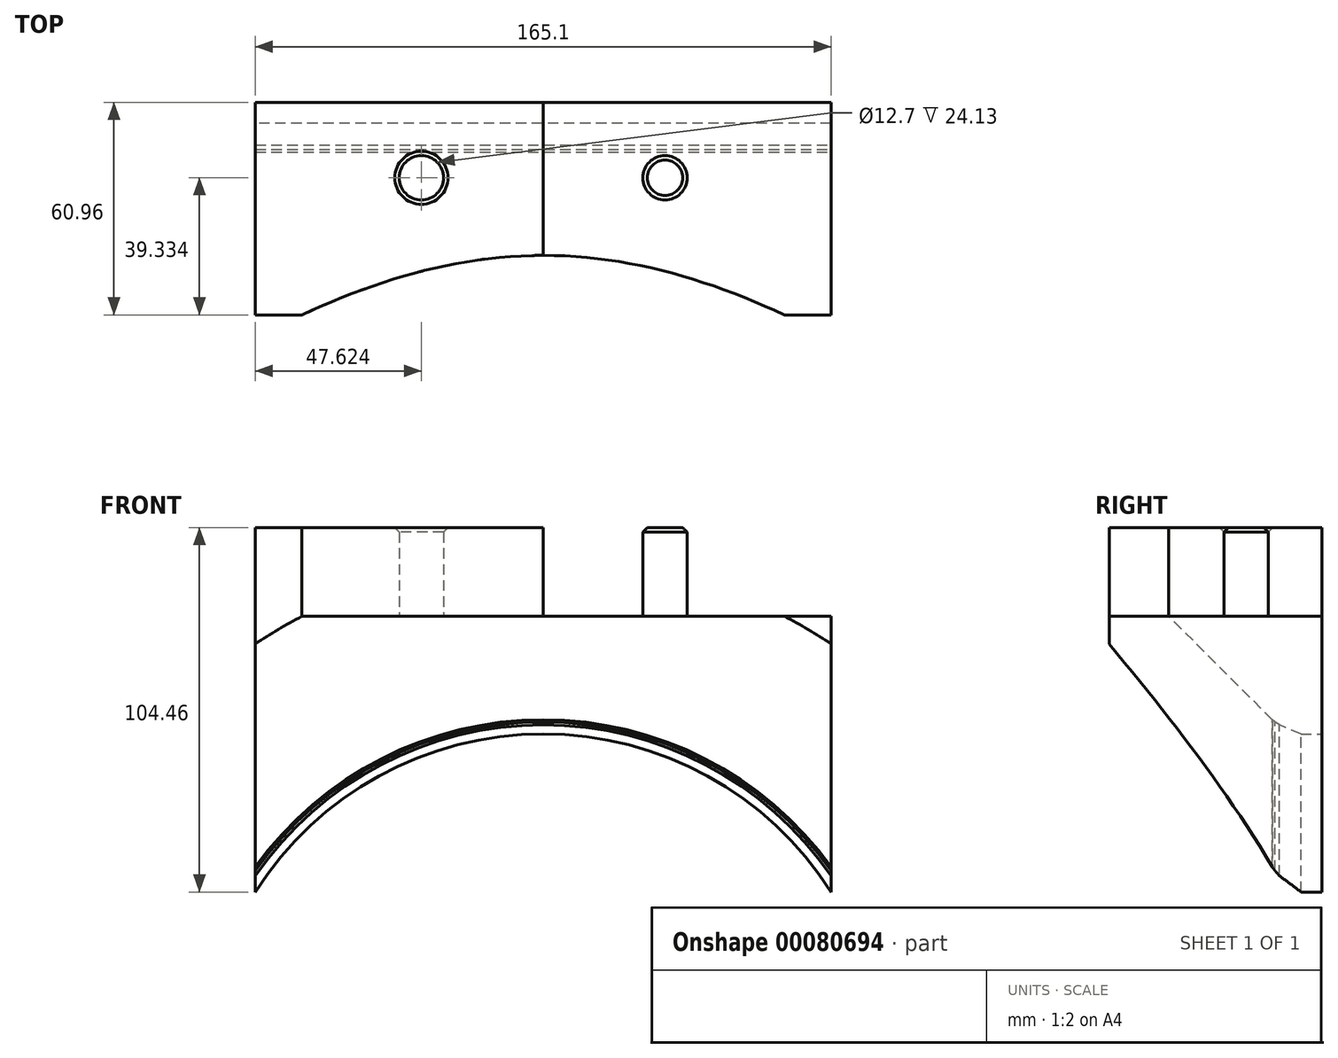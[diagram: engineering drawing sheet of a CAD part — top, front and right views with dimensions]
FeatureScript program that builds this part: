
annotation { "Feature Type Name" : "Feature", "Feature Type Description" : "" }
export const myFeature = defineFeature(function(context is Context, id is Id, definition is map)
    precondition{}
    {
        {
            var Q0;
            Q0=qCreatedBy(makeId("Front.planeOp"),FACE);
            var sketch = newSketch(context, id + "F0", { "sketchPlane" : qUnion([Q0])});
            skLineSegment(sketch, "E0", {"start": v(0, 54.45) * mm, "end": v(-96.4, 54.45) * mm});
            skLineSegment(sketch, "E1", {"start": v(-96.4, 54.45) * mm, "end": v(68.7, 54.45) * mm});
            skLineSegment(sketch, "E2", {"start": v(68.7, 54.45) * mm, "end": v(68.7, -24.61) * mm});
            skLineSegment(sketch, "E3", {"start": v(-96.4, 54.45) * mm, "end": v(-96.4, -24.61) * mm});
            skArc(sketch, "E4", {"start": v(68.7, -24.61) * mm, "mid": v(-13.85, 20.72) * mm, "end": v(-96.4, -24.61) * mm});
            skSolve(sketch);
        }
        {
            var Q0;
            {var subQ2=sQuery(id+"F0.wireOp",EDGE,"E2");Q0=makeQuery(id+"F0.imprint","IMPRINT",FACE,{"disambiguationData":[TD([[makeQuery(id+"F0.imprint","IMPRINT",EDGE,{"derivedFrom":subQ2}),-1.0]])]});}
            extrude(context, id + "F1", {"entities" : qUnion([Q0]), "depth" : 60.96 * mm});
        }
        {
            var Q0;
            Q0=makeQuery(id+"F1.opExtrude","CAP_EDGE",EDGE,{"disambiguationData":[OSD([sQuery(id+"F0.wireOp",EDGE,"E4")])],"isStart":false});
            chamfer(context, id + "F2", {"entities" : qUnion([Q0]), "width" : 50.8 * mm, "tangentPropagation" : true});
        }
        {
            var Q0;
            {var subQ0=sQuery(id+"F0.wireOp",EDGE,"E4");Q0=makeQuery(id+"F2.opChamfer","BLEND_EDGE",EDGE,{"blendedFrom":[makeQuery(id+"F1.opExtrude","CAP_EDGE",EDGE,{"disambiguationData":[OSD([subQ0])],"isStart":false}),makeQuery(id+"F1.opExtrude","SWEPT_FACE",FACE,{"disambiguationData":[OSD([subQ0])]})],"blendedInto":[makeQuery(id+"F1.opExtrude","SWEPT_FACE",FACE,{"disambiguationData":[OSD([subQ0])]})]});}
            chamfer(context, id + "F3", {"entities" : qUnion([Q0]), "width" : 10.16 * mm, "tangentPropagation" : true});
        }
        {
            var Q0;
            Q0=makeQuery(id+"F1.opExtrude","SWEPT_FACE",FACE,{"disambiguationData":[OSD([sQuery(id+"F0.wireOp",EDGE,"E1")])]});
            var sketch = newSketch(context, id + "F4", { "sketchPlane" : qUnion([Q0])});
            skCircle(sketch, "E5", {"center": v(21.07, -21.63) * mm, "radius": 6.35 * mm});
            skLineSegment(sketch, "E6", {"start": v(-13.85, 0) * mm, "end": v(-13.85, -43.88) * mm});
            skCircle(sketch, "E7.MirrorC", {"center": v(-48.78, -21.63) * mm, "radius": 6.35 * mm});
            skSolve(sketch);
        }
        {
            var Q0;
            Q0=makeQuery(id+"F4.imprint","IMPRINT",FACE,{"disambiguationData":[TD([[makeQuery(id+"F4.imprint","IMPRINT",EDGE,{"derivedFrom":sQuery(id+"F4.wireOp",EDGE,"E7.MirrorC")}),-1.0]])]});
            var Q1;
            Q1=makeQuery(id+"F4.imprint","IMPRINT",FACE,{"disambiguationData":[TD([[makeQuery(id+"F4.imprint","IMPRINT",EDGE,{"derivedFrom":sQuery(id+"F4.wireOp",EDGE,"E5")}),1.0]])]});
            extrude(context, id + "F5", {"entities" : qUnion([Q0, Q1]), "operationType" : NewBodyOperationType.ADD, "depth" : 25.4 * mm});
        }
        {
            var Q0;
            Q0=makeQuery(id+"F5.opExtrude","CAP_EDGE",EDGE,{"disambiguationData":[OSD([sQuery(id+"F4.wireOp",EDGE,"E7.MirrorC")])],"isStart":false});
            var Q1;
            Q1=makeQuery(id+"F5.opExtrude","CAP_EDGE",EDGE,{"disambiguationData":[OSD([sQuery(id+"F4.wireOp",EDGE,"E5")])],"isStart":false});
            chamfer(context, id + "F6", {"entities" : qUnion([Q0, Q1]), "width" : 1.27 * mm, "tangentPropagation" : true});
        }
        {
            var Q0;
            {var subQ0=sQuery(id+"F0.wireOp",EDGE,"E4");Q0=makeQuery(id+"F3.opChamfer","BLEND_EDGE",EDGE,{"blendedFrom":[makeQuery(id+"F2.opChamfer","BLEND_EDGE",EDGE,{"blendedFrom":[makeQuery(id+"F1.opExtrude","CAP_EDGE",EDGE,{"disambiguationData":[OSD([subQ0])],"isStart":false}),makeQuery(id+"F1.opExtrude","SWEPT_FACE",FACE,{"disambiguationData":[OSD([subQ0])]})],"blendedInto":[makeQuery(id+"F1.opExtrude","SWEPT_FACE",FACE,{"disambiguationData":[OSD([subQ0])]})]}),makeQuery(id+"F2.opChamfer","BLEND_FACE",FACE,{"disambiguationData":[OSD([subQ0])]})],"blendedInto":[makeQuery(id+"F2.opChamfer","BLEND_FACE",FACE,{"disambiguationData":[OSD([subQ0])]})]});}
            chamfer(context, id + "F7", {"entities" : qUnion([Q0]), "width" : 5.08 * mm, "tangentPropagation" : true});
        }
        {
            var Q0;
            {var subQ0=sQuery(id+"F0.wireOp",EDGE,"E4");var subQ1=makeQuery(id+"F2.opChamfer","BLEND_FACE",FACE,{"disambiguationData":[OSD([subQ0])]});Q0=makeQuery(id+"F7.opChamfer","BLEND_EDGE",EDGE,{"blendedFrom":[makeQuery(id+"F3.opChamfer","BLEND_EDGE",EDGE,{"blendedFrom":[makeQuery(id+"F2.opChamfer","BLEND_EDGE",EDGE,{"blendedFrom":[makeQuery(id+"F1.opExtrude","CAP_EDGE",EDGE,{"disambiguationData":[OSD([subQ0])],"isStart":false}),makeQuery(id+"F1.opExtrude","SWEPT_FACE",FACE,{"disambiguationData":[OSD([subQ0])]})],"blendedInto":[makeQuery(id+"F1.opExtrude","SWEPT_FACE",FACE,{"disambiguationData":[OSD([subQ0])]})]}),subQ1],"blendedInto":[subQ1]}),subQ1],"blendedInto":[subQ1]});}
            chamfer(context, id + "F8", {"entities" : qUnion([Q0]), "width" : 5.08 * mm, "tangentPropagation" : true});
        }
    });
